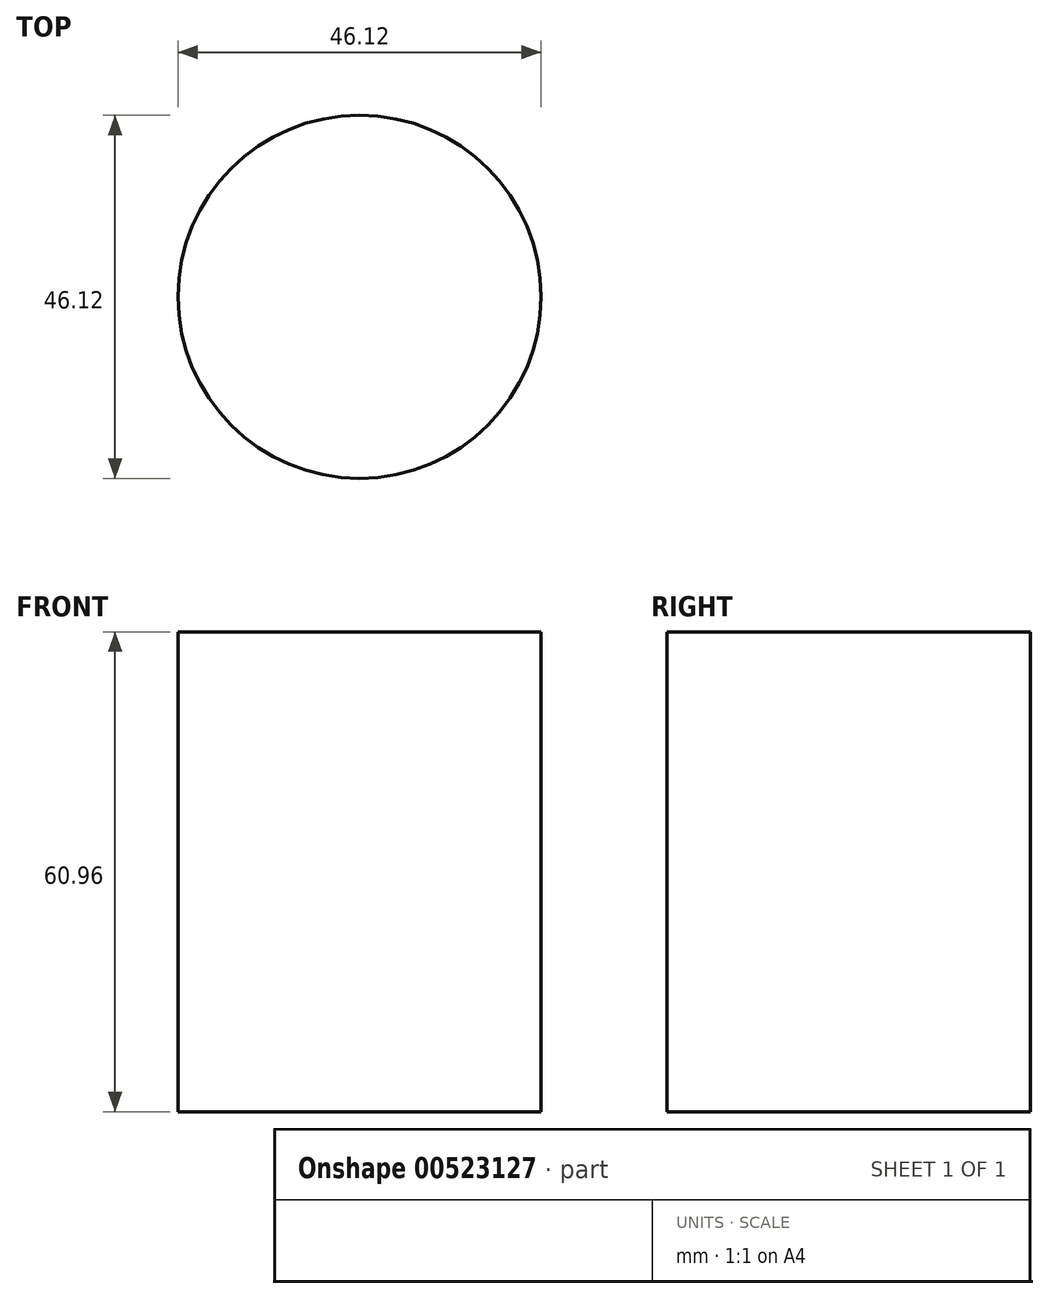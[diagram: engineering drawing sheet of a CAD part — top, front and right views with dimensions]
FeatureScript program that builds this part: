
annotation { "Feature Type Name" : "Feature", "Feature Type Description" : "" }
export const myFeature = defineFeature(function(context is Context, id is Id, definition is map)
    precondition{}
    {
        {
            var Q0;
            Q0=qCreatedBy(makeId("Top.planeOp"),FACE);
            var sketch = newSketch(context, id + "F0", { "sketchPlane" : qUnion([Q0])});
            skCircle(sketch, "E0", {"center": v(0, 0) * mm, "radius": 23.06 * mm});
            skSolve(sketch);
        }
        {
            var Q0;
            Q0 = qSketchRegion(id + "F0", true);
            extrude(context, id + "F1", {"entities" : qUnion([Q0]), "depth" : 60.96 * mm, "offsetDistance" : 25.4 * mm});
        }
    });
